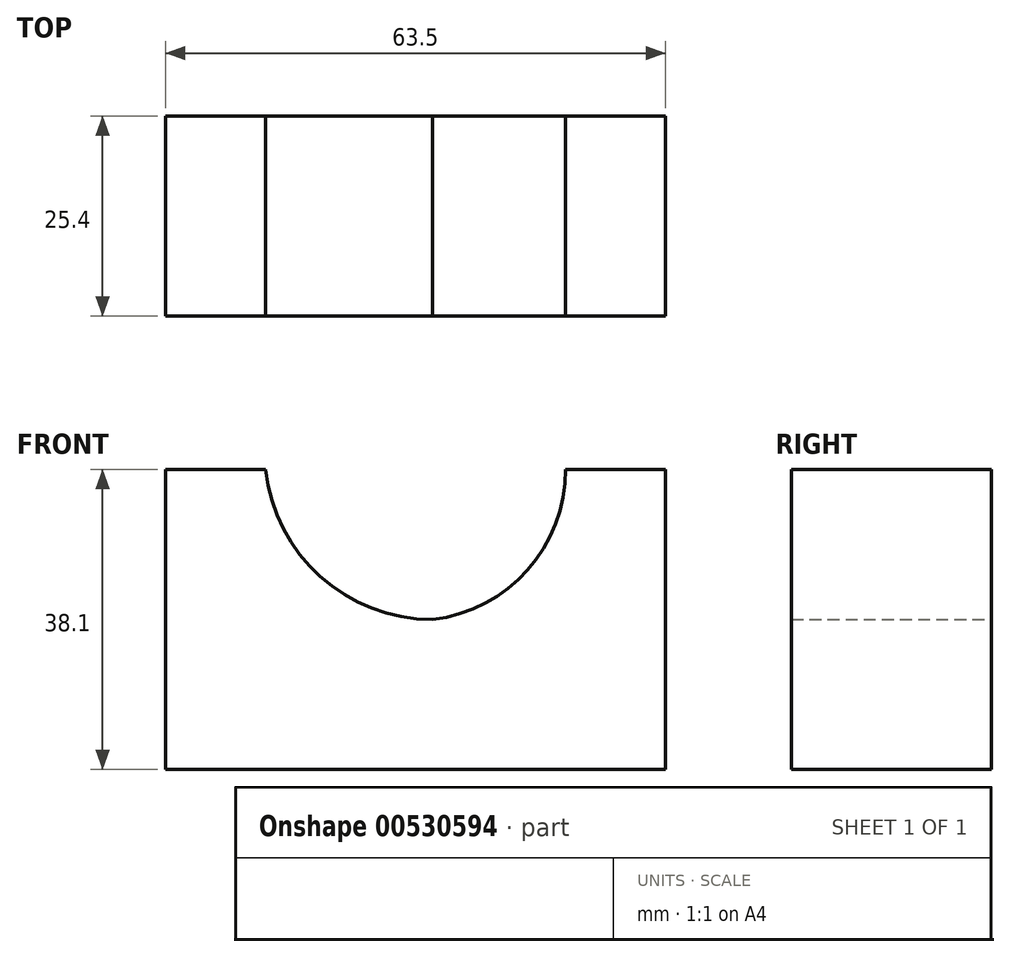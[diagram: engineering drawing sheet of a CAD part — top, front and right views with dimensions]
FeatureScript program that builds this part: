
annotation { "Feature Type Name" : "Feature", "Feature Type Description" : "" }
export const myFeature = defineFeature(function(context is Context, id is Id, definition is map)
    precondition{}
    {
        {
            var Q0;
            Q0=qCreatedBy(makeId("Front.planeOp"),FACE);
            var sketch = newSketch(context, id + "F0", { "sketchPlane" : qUnion([Q0])});
            skLineSegment(sketch, "E0", {"start": v(-40.04, 38.1) * mm, "end": v(23.46, 38.1) * mm});
            skLineSegment(sketch, "E1", {"start": v(23.46, 38.1) * mm, "end": v(23.46, 0) * mm});
            skLineSegment(sketch, "E2", {"start": v(23.46, 0) * mm, "end": v(-40.04, 0) * mm});
            skLineSegment(sketch, "E3", {"start": v(-40.04, 0) * mm, "end": v(-40.04, 38.1) * mm});
            skArc(sketch, "E4", {"start": v(-6.14, 19.05) * mm, "mid": v(5.96, 25.34) * mm, "end": v(10.76, 38.1) * mm});
            skArc(sketch, "E5", {"start": v(-27.34, 38.1) * mm, "mid": v(-20.39, 24.51) * mm, "end": v(-6.14, 19.05) * mm});
            skSolve(sketch);
        }
        {
            var Q0;
            {var subQ0=sQuery(id+"F0.wireOp",EDGE,"E1");Q0=makeQuery(id+"F0.imprint","IMPRINT",FACE,{"disambiguationData":[TD([[makeQuery(id+"F0.imprint","IMPRINT",EDGE,{"derivedFrom":subQ0}),-1.0]])]});}
            extrude(context, id + "F1", {"entities" : qUnion([Q0]), "depth" : 25.4 * mm, "offsetDistance" : 25.4 * mm});
        }
    });
